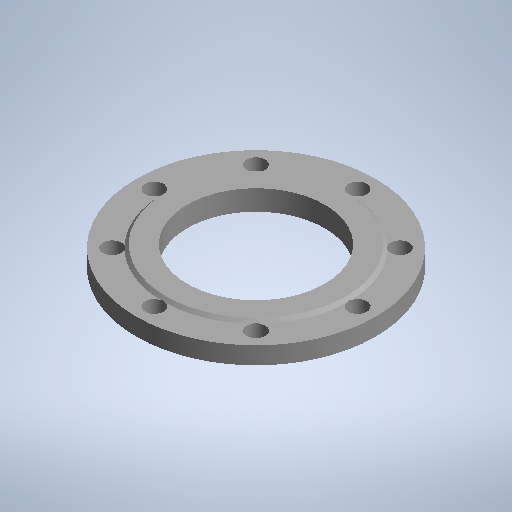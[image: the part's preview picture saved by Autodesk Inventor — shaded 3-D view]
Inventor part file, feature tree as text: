
AUTODESK INVENTOR PART (.ipt)
format: ipt  version: 2025 (Build 290162010, 162A)  size: 264,704 bytes
history: native  units: mm (DEFAULTED — no unit token found)
features: sketch x2, revolve x1, chamfer x1, hole x1, pattern_circular x1
ambient origin geometry x8: Origin, YZ Plane, XZ Plane, XY Plane, X Axis, Y Axis, Z Axis, Center Point
bodies: Solid1 (feature_tree)
feature tree (6):
  revolve  "Revolution1"  [1 undecoded]
  chamfer  "Chamfer1"  Distance=17.0mm
  hole  "Hole1"  [1 undecoded]
  pattern_circular  "Circular Pattern1"  Angle=90.0deg  [1 undecoded]
  sketch  "Sketch1"  dims[d0=50.0mm d1=24.0mm]
  sketch  "Sketch2"  dims[d2=135.0mm d3=17.0mm d4=20.0mm d5=90.0deg d6=3.0mm d7=2.0mm d8=45.0deg d9=200.0mm d10=18.0mm d11=6.0mm d12=4.0mm d13=2.0mm d14=90.0deg d15=8.0mm d16=20.594885mm d17=80.0mm d18=360.0deg]
note: 3 required parameter values undecoded (feature->parameter linkage not recoverable at this tier; creation-order binding heuristic only, values carry confidence <= 0.55)